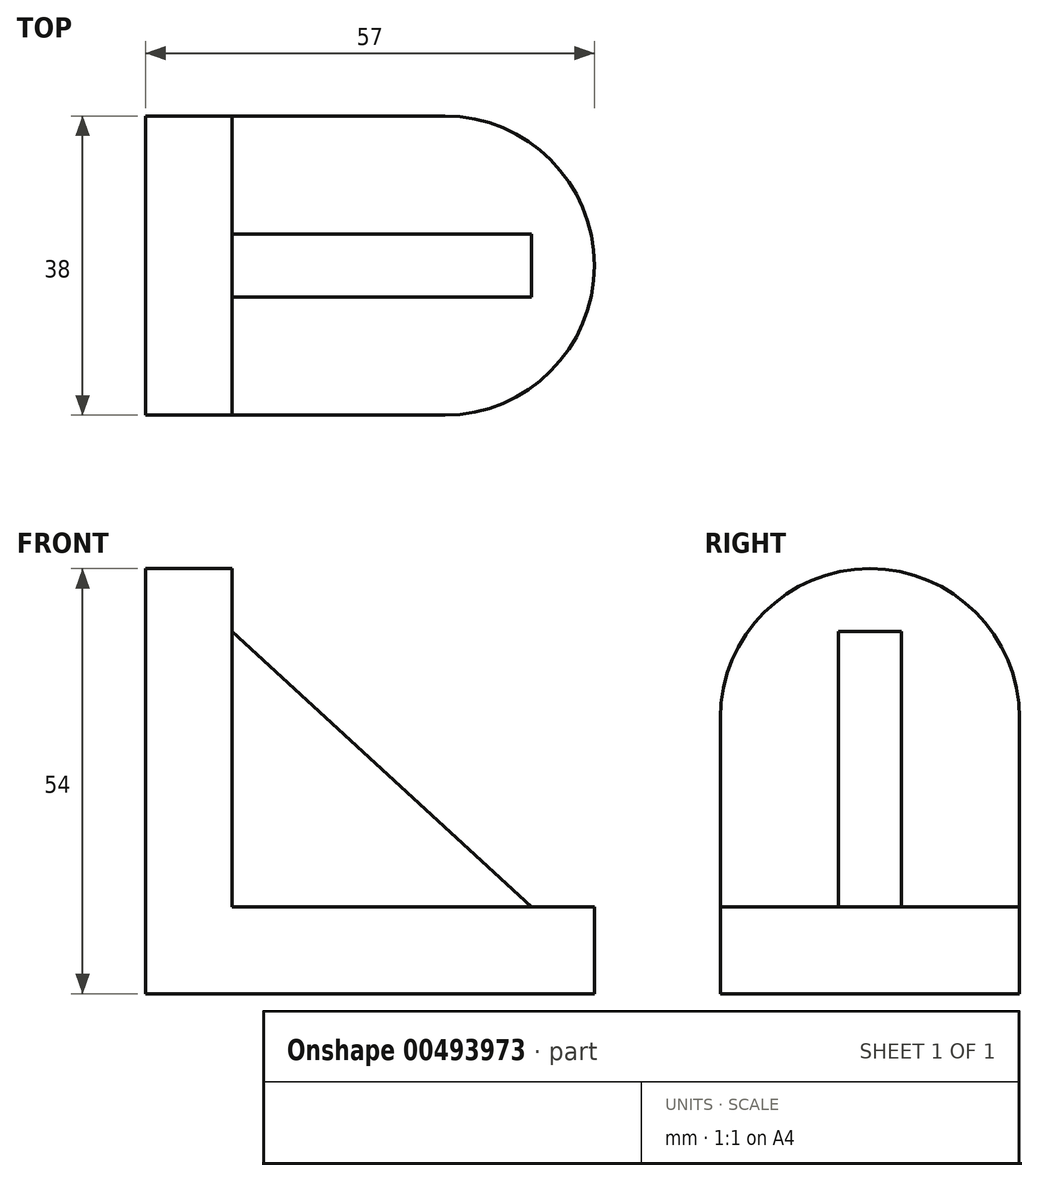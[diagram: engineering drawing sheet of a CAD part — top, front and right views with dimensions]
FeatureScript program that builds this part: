
annotation { "Feature Type Name" : "Feature", "Feature Type Description" : "" }
export const myFeature = defineFeature(function(context is Context, id is Id, definition is map)
    precondition{}
    {
        {
            var Q0;
            Q0=qCreatedBy(makeId("Front.planeOp"),FACE);
            var sketch = newSketch(context, id + "F0", { "sketchPlane" : qUnion([Q0])});
            skLineSegment(sketch, "E0", {"start": v(0, 0) * mm, "end": v(0, 54) * mm});
            skLineSegment(sketch, "E1", {"start": v(0, 54) * mm, "end": v(11, 54) * mm});
            skLineSegment(sketch, "E2", {"start": v(11, 54) * mm, "end": v(11, 11) * mm});
            skLineSegment(sketch, "E3", {"start": v(11, 11) * mm, "end": v(57, 11) * mm});
            skLineSegment(sketch, "E4", {"start": v(57, 11) * mm, "end": v(57, 0) * mm});
            skLineSegment(sketch, "E5", {"start": v(57, 0) * mm, "end": v(0, 0) * mm});
            skSolve(sketch);
        }
        {
            var Q0;
            Q0 = qSketchRegion(id + "F0", true);
            extrude(context, id + "F1", {"entities" : qUnion([Q0]), "endBound" : BoundingType.SYMMETRIC, "depth" : 38 * mm});
        }
        {
            var Q0;
            Q0=makeQuery(id+"F1.opExtrude","CAP_EDGE",EDGE,{"disambiguationData":[OSD([sQuery(id+"F0.wireOp",EDGE,"E1")])],"isStart":false});
            var Q1;
            Q1=makeQuery(id+"F1.opExtrude","CAP_EDGE",EDGE,{"disambiguationData":[OSD([sQuery(id+"F0.wireOp",EDGE,"E1")])],"isStart":true});
            var Q2;
            Q2=makeQuery(id+"F1.opExtrude","CAP_EDGE",EDGE,{"disambiguationData":[OSD([sQuery(id+"F0.wireOp",EDGE,"E4")])],"isStart":false});
            var Q3;
            Q3=makeQuery(id+"F1.opExtrude","CAP_EDGE",EDGE,{"disambiguationData":[OSD([sQuery(id+"F0.wireOp",EDGE,"E4")])],"isStart":true});
            fillet(context, id + "F2", {"entities" : qUnion([Q0, Q1, Q2, Q3]), "radius" : 19 * mm, "tangentPropagation" : true, "allowEdgeOverflow" : false});
        }
        {
            var Q0;
            Q0=qCreatedBy(makeId("Front.planeOp"),FACE);
            var sketch = newSketch(context, id + "F3", { "sketchPlane" : qUnion([Q0])});
            skLineSegment(sketch, "E6", {"start": v(11, 46) * mm, "end": v(49, 11) * mm});
            skLineSegment(sketch, "E7.0", {"start": v(11, 35) * mm, "end": v(11, 54) * mm});
            skLineSegment(sketch, "E8.0.0", {"start": v(38, 0) * mm, "end": v(57, 0) * mm});
            skLineSegment(sketch, "E8.0.1", {"start": v(38, 0) * mm, "end": v(38, 11) * mm});
            skLineSegment(sketch, "E8.0.2", {"start": v(38, 11) * mm, "end": v(57, 11) * mm});
            skLineSegment(sketch, "E8.0.3", {"start": v(38, 0) * mm, "end": v(38, 11) * mm});
            skLineSegment(sketch, "E9", {"start": v(11, 46) * mm, "end": v(11, 11) * mm});
            skLineSegment(sketch, "E10", {"start": v(49, 11) * mm, "end": v(11, 11) * mm});
            skSolve(sketch);
        }
        {
            var Q0;
            Q0 = qSketchRegion(id + "F3", true);
            extrude(context, id + "F4", {"entities" : qUnion([Q0]), "operationType" : NewBodyOperationType.ADD, "endBound" : BoundingType.SYMMETRIC, "depth" : 8 * mm});
        }
    });
